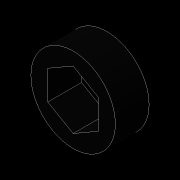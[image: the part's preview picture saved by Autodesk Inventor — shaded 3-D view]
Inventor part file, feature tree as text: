
AUTODESK INVENTOR PART (.ipt)
format: ipt  version: 2016 (Build 200138000, 138)  size: 80,896 bytes
history: native  units: in
note: dims shown in document units (in); Inventor stores cm internally (conversion verified against a paired STEP export)
features: extrude x1, sketch x1
ambient origin geometry x8: Origin, YZ Plane, XZ Plane, XY Plane, X Axis, Y Axis, Z Axis, Center Point
bodies: Solid1 (feature_tree)
feature tree (2):
  extrude  "Extrusion1"  Depth=0.25in
  sketch  "Sketch1"  dims[d0=0.375in d1=0.625in d2=0.25in d3=0.0in]
